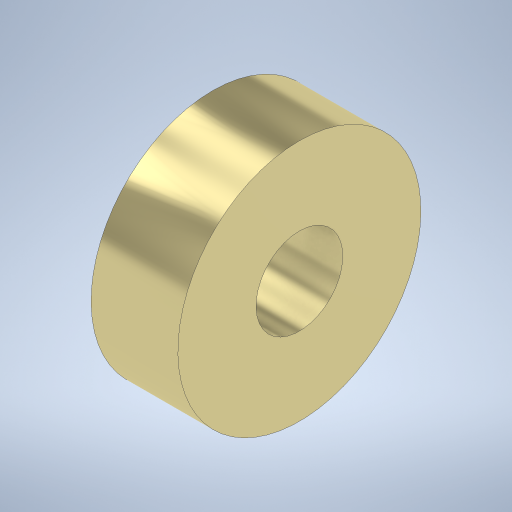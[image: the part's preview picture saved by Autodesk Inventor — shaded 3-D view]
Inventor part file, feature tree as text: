
AUTODESK INVENTOR PART (.ipt)
format: ipt  version: 2024 (Build 280153020, 153B)  size: 239,616 bytes
history: native  units: mm
features: extrude x1, sketch x1
ambient origin geometry x8: Origin, YZ Plane, XZ Plane, XY Plane, X Axis, Y Axis, Z Axis, Center Point
bodies: Solid1 (feature_tree)
feature tree (2):
  extrude  "Extrusion1"  Depth=5.0mm
  sketch  "Sketch1"  dims[d0=5.0mm d1=14.0mm d2=5.0mm d3=0.0mm]
